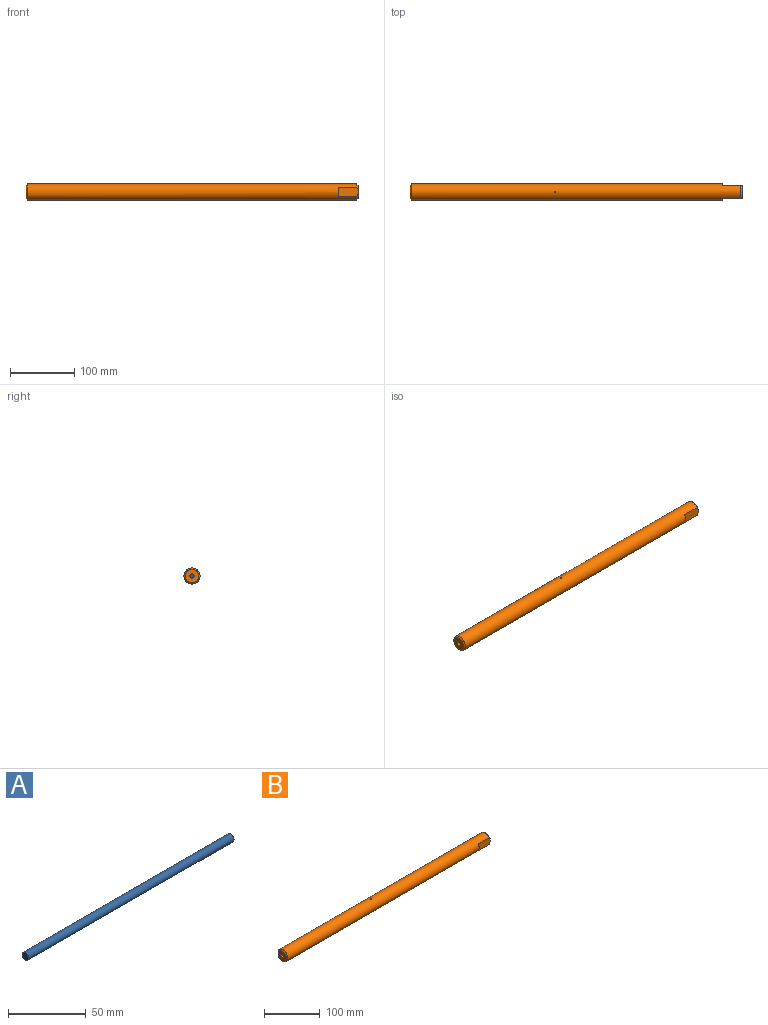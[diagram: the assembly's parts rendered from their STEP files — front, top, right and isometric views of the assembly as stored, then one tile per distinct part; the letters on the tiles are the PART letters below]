
ASSEMBLY  parts=2 mates=1
PART A: 3 faces, bbox 187x6x6 mm
  f0: plane 6x6mm, normal (-1,0,0), area 28.3mm2, adj f2
  f1: plane 6x6mm, normal (1,0,0), area 28.3mm2, adj f2
  f2: cylinder r=3mm len=187mm, axis (-1,0,0), area 3524.9mm2, adj f0,f1
PART B: 17 faces, bbox 515x25x25 mm
  f0: cylinder r=12.5mm len=511mm, axis (1,0,0), area 39229.8mm2, adj f4,f5,f6,f7,f8,f9,f10,f14
  f1: cylinder r=3.25mm len=211.16mm, axis (1,0,0), area 4308.8mm2, adj f11,f13,f14
  f2: plane 21x20mm, normal (1,0,0), area 305.8mm2, adj f5,f7,f9,f10,f16
  f3: plane 21x21mm, normal (-1,0,0), area 310mm2, adj f8,f12
  f4: plane 15x2.5mm, normal (1,0,0), area 25.5mm2, adj f0,f5
  f5: plane 30x15mm, normal (0,-1,0), area 442.3mm2, adj f0,f2,f4,f9,f10
  f6: plane 15x2.5mm, normal (1,0,0), area 25.5mm2, adj f0,f7
  f7: plane 30x15mm, normal (0,1,0), area 442.3mm2, adj f0,f2,f6,f9,f10
  f8: cone r=12.5mm half-angle=45deg, axis (1,0,0), area 204.4mm2, adj f0,f3
  f9: cone r=10.5mm half-angle=45deg, axis (-1,0,0), area 69.1mm2, adj f0,f2,f5,f7
  f10: cone r=10.5mm half-angle=45deg, axis (-1,0,0), area 69.1mm2, adj f0,f2,f5,f7
  f11: cone r=0mm half-angle=59deg, axis (-1,0,0), area 3.7mm2, adj f1,f12
  f12: cylinder r=3.4mm len=18.75mm, axis (-1,0,0), area 400.6mm2, adj f3,f11
  f13: cone r=0mm half-angle=60deg, axis (-1,0,0), area 38.3mm2, adj f1
  f14: cylinder r=1mm len=9.41mm, axis (0,0,-1), area 58.5mm2, adj f0,f1
  f15: cone r=0mm half-angle=59deg, axis (1,0,0), area 42.4mm2, adj f16
  f16: cylinder r=3.4mm len=28.75mm, axis (1,0,0), area 614.2mm2, adj f2,f15
PLACE A t=(-112.89,48.93,-35.59)mm
PLACE B t=(-131.64,48.93,-35.59)mm
MATE fastened A.f2 <-> B.f0  axis (-1,0,0) through (-112.89,48.93,-35.59)mm
